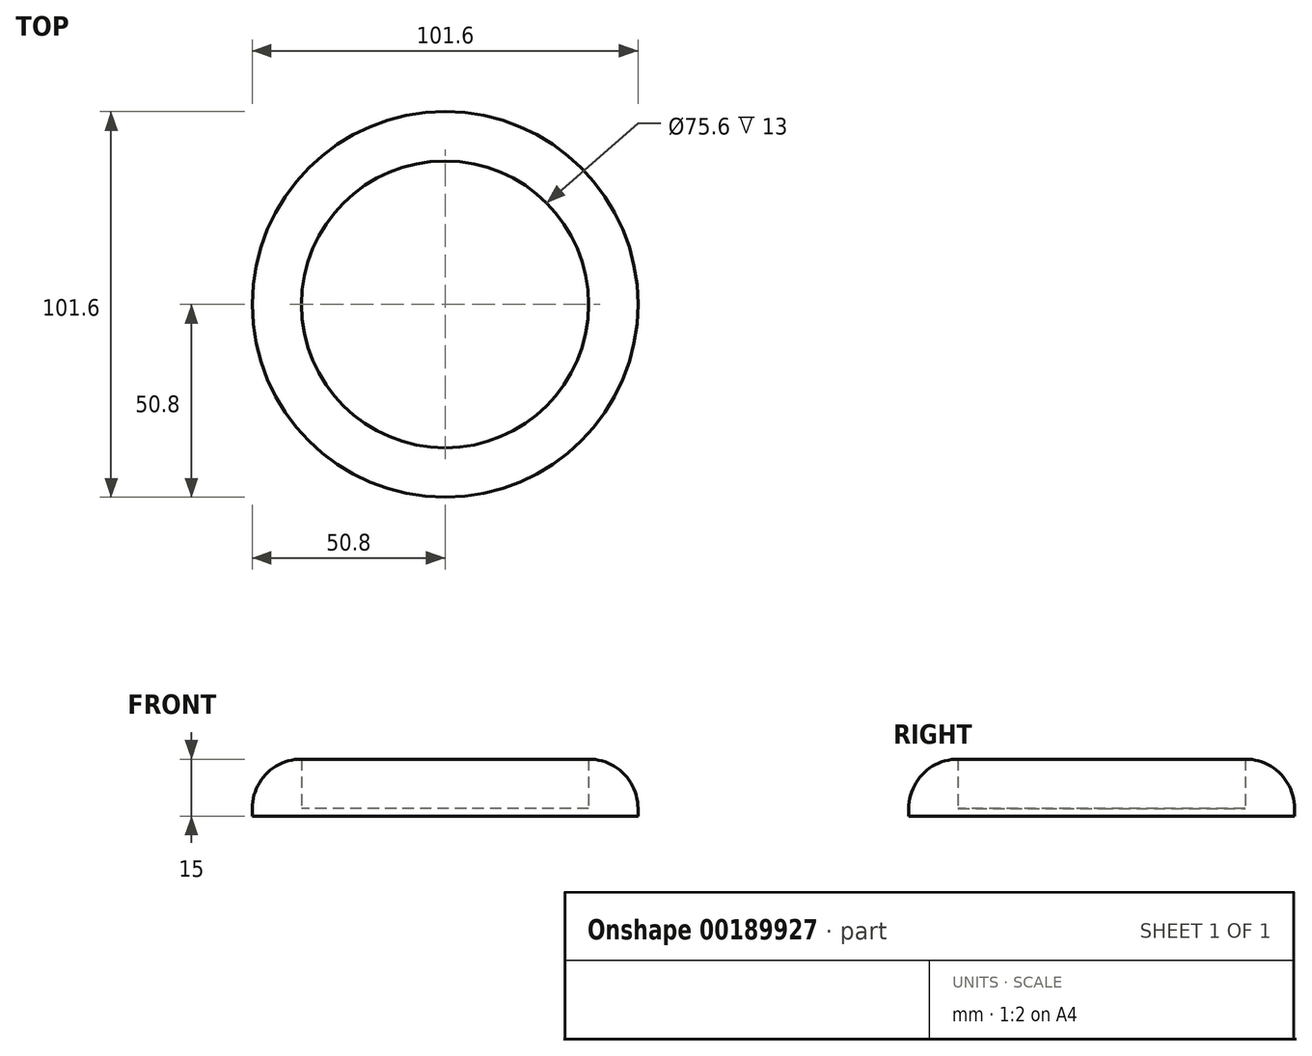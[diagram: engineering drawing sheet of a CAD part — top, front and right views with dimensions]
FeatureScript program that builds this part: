
annotation { "Feature Type Name" : "Feature", "Feature Type Description" : "" }
export const myFeature = defineFeature(function(context is Context, id is Id, definition is map)
    precondition{}
    {
        {
            var Q0;
            Q0=qCreatedBy(makeId("Top.planeOp"),FACE);
            var sketch = newSketch(context, id + "F0", { "sketchPlane" : qUnion([Q0])});
            skCircle(sketch, "E0", {"center": v(0, 0) * mm, "radius": 37.8 * mm});
            skCircle(sketch, "E1.0", {"center": v(0, 0) * mm, "radius": 50.8 * mm});
            skSolve(sketch);
        }
        {
            var Q0;
            Q0=makeQuery(id+"F0.imprint","IMPRINT",FACE,{"disambiguationData":[TD([[makeQuery(id+"F0.imprint","IMPRINT",EDGE,{"derivedFrom":sQuery(id+"F0.wireOp",EDGE,"E0")}),-1.0]])]});
            var Q1;
            Q1=makeQuery(id+"F0.imprint","IMPRINT",FACE,{"disambiguationData":[TD([[makeQuery(id+"F0.imprint","IMPRINT",EDGE,{"derivedFrom":sQuery(id+"F0.wireOp",EDGE,"E0")}),1.0]])]});
            extrude(context, id + "F1", {"entities" : qUnion([Q0, Q1]), "oppositeDirection" : true, "depth" : 2 * mm});
        }
        {
            var Q0;
            Q0=makeQuery(id+"F0.imprint","IMPRINT",FACE,{"disambiguationData":[TD([[makeQuery(id+"F0.imprint","IMPRINT",EDGE,{"derivedFrom":sQuery(id+"F0.wireOp",EDGE,"E0")}),-1.0]])]});
            extrude(context, id + "F2", {"entities" : qUnion([Q0]), "operationType" : NewBodyOperationType.ADD, "depth" : 13 * mm});
        }
        {
            var Q0;
            Q0=makeQuery(id+"F2.opExtrude","CAP_EDGE",EDGE,{"disambiguationData":[OSD([sQuery(id+"F0.wireOp",EDGE,"E1.0")])],"isStart":false});
            fillet(context, id + "F3", {"entities" : qUnion([Q0]), "radius" : 13 * mm, "tangentPropagation" : true, "allowEdgeOverflow" : false});
        }
    });
